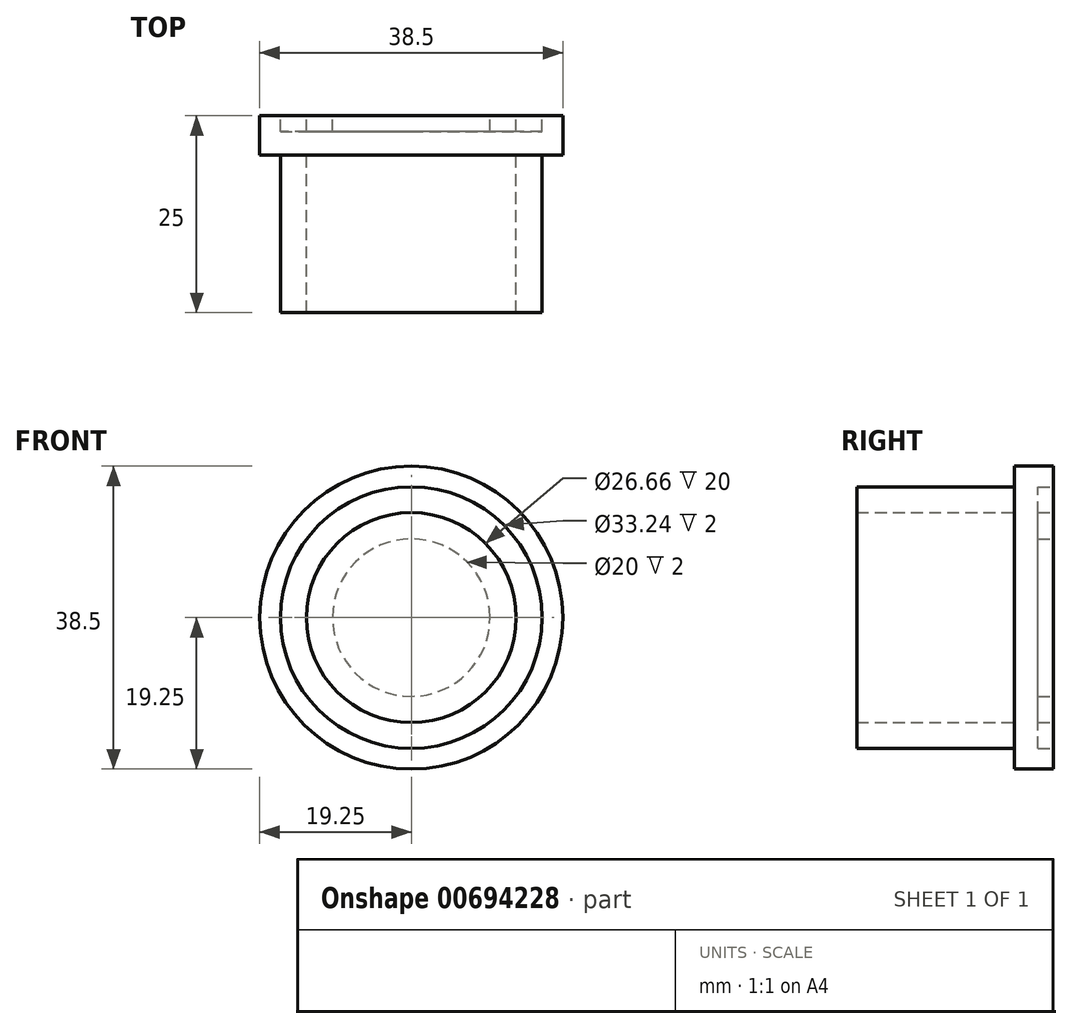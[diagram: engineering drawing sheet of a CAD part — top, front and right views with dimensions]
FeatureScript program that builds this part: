
annotation { "Feature Type Name" : "Feature", "Feature Type Description" : "" }
export const myFeature = defineFeature(function(context is Context, id is Id, definition is map)
    precondition{}
    {
        {
            var Q0;
            Q0=qCreatedBy(makeId("Front.planeOp"),FACE);
            var sketch = newSketch(context, id + "F0", { "sketchPlane" : qUnion([Q0])});
            skCircle(sketch, "E0", {"center": v(0, 0) * mm, "radius": 19.25 * mm});
            skSolve(sketch);
        }
        {
            var Q0;
            Q0=qCreatedBy(makeId("Front.planeOp"),FACE);
            var sketch = newSketch(context, id + "F1", { "sketchPlane" : qUnion([Q0])});
            skCircle(sketch, "E1", {"center": v(0, 0) * mm, "radius": 10 * mm});
            skCircle(sketch, "E2", {"center": v(0, 0) * mm, "radius": 16.62 * mm});
            skCircle(sketch, "E3", {"center": v(0, 0) * mm, "radius": 13.33 * mm});
            skSolve(sketch);
        }
        {
            var Q0;
            Q0 = qSketchRegion(id + "F0", true);
            extrude(context, id + "F2", {"entities" : qUnion([Q0]), "depth" : 5 * mm, "offsetDistance" : 25 * mm});
        }
        {
            var Q0;
            Q0=makeQuery(id+"F1.imprint","IMPRINT",FACE,{"disambiguationData":[TD([[makeQuery(id+"F1.imprint","IMPRINT",EDGE,{"derivedFrom":sQuery(id+"F1.wireOp",EDGE,"E1")}),1.0]])]});
            extrude(context, id + "F3", {"entities" : qUnion([Q0]), "operationType" : NewBodyOperationType.REMOVE, "depth" : 2 * mm, "offsetDistance" : 25 * mm});
        }
        {
            var Q0;
            Q0=makeQuery(id+"F1.imprint","IMPRINT",FACE,{"disambiguationData":[TD([[makeQuery(id+"F1.imprint","IMPRINT",EDGE,{"derivedFrom":sQuery(id+"F1.wireOp",EDGE,"E2")}),1.0]])]});
            extrude(context, id + "F4", {"entities" : qUnion([Q0]), "operationType" : NewBodyOperationType.ADD, "depth" : 25 * mm, "offsetDistance" : 25 * mm});
        }
        {
            var Q0;
            Q0=makeQuery(id+"F1.imprint","IMPRINT",FACE,{"disambiguationData":[TD([[makeQuery(id+"F1.imprint","IMPRINT",EDGE,{"derivedFrom":sQuery(id+"F1.wireOp",EDGE,"E2")}),1.0]])]});
            extrude(context, id + "F5", {"entities" : qUnion([Q0]), "operationType" : NewBodyOperationType.REMOVE, "depth" : 2 * mm, "offsetDistance" : 25 * mm});
        }
    });
